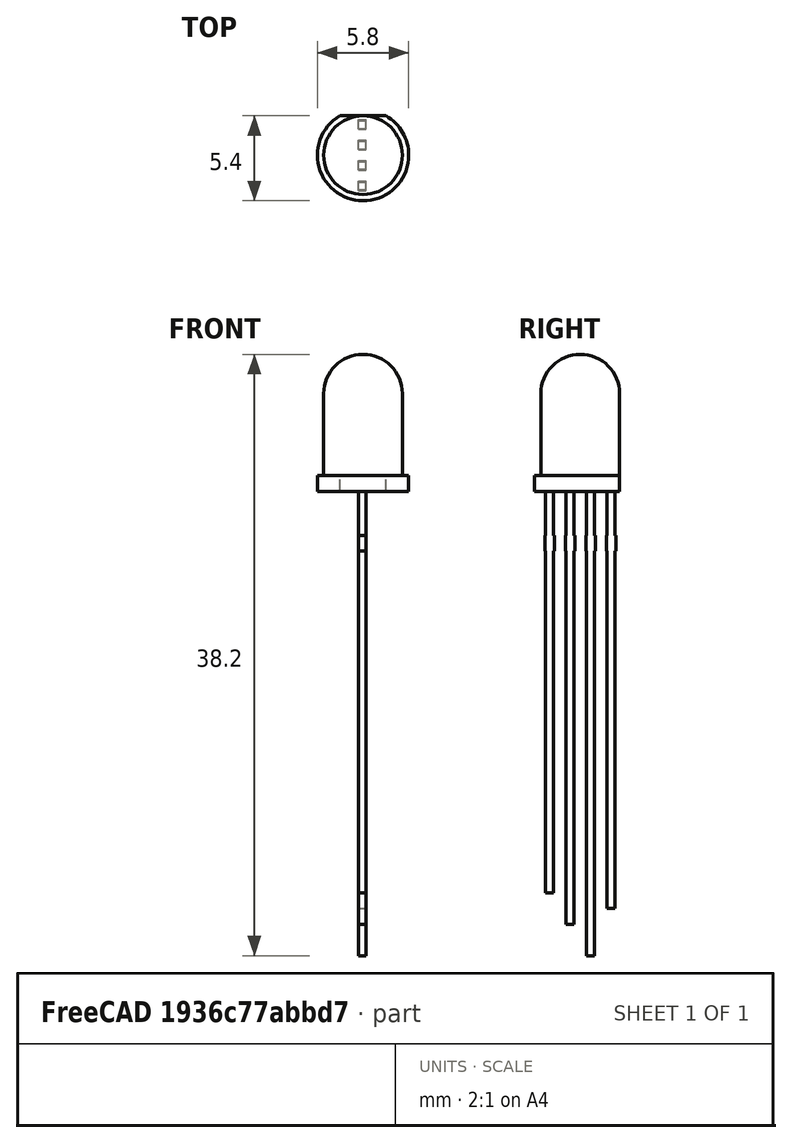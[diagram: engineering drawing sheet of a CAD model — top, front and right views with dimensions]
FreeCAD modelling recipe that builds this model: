
FCSTD DOCUMENT  (FreeCAD 0.16R6703 (Git))
Label: RGB-LED-5mm
License: All rights reserved
LicenseURL: http://en.wikipedia.org/wiki/All_rights_reserved
objects: Part::Box×9, Part::MultiFuse×5, Part::Cylinder×2, Part::Sphere×1, Part::Cut×1
note: 18 computed .brp shape members not serialized (recipe doc carries the construction recipe); baked Part::Feature solids carry a one-line shape summary decoded from their .brp

FEATURE [Part::Cylinder] Cylinder  label="Cilindro"
  Angle = 360
  Height = 5.2
  Placement = pos=(0,0,4.8) rot=(0,0,1;0rad)
  Radius = 2.5
FEATURE [Part::Sphere] Sphere  label="Esfera"
  Angle1 = 0
  Angle2 = 90
  Angle3 = 360
  Placement = pos=(0,0,10) rot=(0,0,1;0rad)
  Radius = 2.5
FEATURE [Part::Cylinder] Cylinder001  label="Cilindro001"
  Angle = 360
  Height = 1
  Placement = pos=(0,0,3.8) rot=(0,0,1;0rad)
  Radius = 2.9
FEATURE [Part::Box] Box  label="Cubo"
  Height = 3
  Length = 13
  Placement = pos=(-4.5,2.5,3) rot=(0,0,1;0rad)
  Width = 2
FEATURE [Part::Box] Box001  label="Cubo001"
  Height = 26.5
  Length = 0.5
  Placement = pos=(0,1.7,-22.7) rot=(0,0,1;0rad)
  Width = 0.5
FEATURE [Part::Box] Box002  label="Cubo002"
  Height = 1
  Length = 0.5
  Placement = pos=(0,1.65,0) rot=(0,0,1;0rad)
  Width = 0.6
FEATURE [Part::Box] Box003  label="GND"
  Height = 29.5
  Length = 0.5
  Placement = pos=(0,0.4,-25.7) rot=(0,0,1;0rad)
  Width = 0.5
FEATURE [Part::Box] Box004  label="Cubo004"
  Height = 27.5
  Length = 0.5
  Placement = pos=(0,-0.9,-23.7) rot=(0,0,1;0rad)
  Width = 0.5
FEATURE [Part::Box] Box005  label="Cubo005"
  Height = 25.5
  Length = 0.5
  Placement = pos=(0,-2.2,-21.7) rot=(0,0,1;0rad)
  Width = 0.5
FEATURE [Part::Cut] Cut  label="Pieza"
  Base = -> Cylinder001
  Tool = -> Box
FEATURE [Part::Box] Box006  label="Cubo006"
  Height = 1
  Length = 0.5
  Placement = pos=(0,0.35,0) rot=(0,0,1;0rad)
  Width = 0.6
FEATURE [Part::Box] Box007  label="Cubo007"
  Height = 1
  Length = 0.5
  Placement = pos=(0,-0.95,0) rot=(0,0,1;0rad)
  Width = 0.6
FEATURE [Part::Box] Box008  label="Cubo008"
  Height = 1
  Length = 0.5
  Placement = pos=(0,-2.25,0) rot=(0,0,1;0rad)
  Width = 0.6
FEATURE [Part::MultiFuse] Fusion  label="Red"
  Shapes = -> [Box001,Box002]
FEATURE [Part::MultiFuse] Fusion001  label="GND001"
  Shapes = -> [Box003,Box006]
FEATURE [Part::MultiFuse] Fusion002  label="Green"
  Shapes = -> [Box004,Box007]
FEATURE [Part::MultiFuse] Fusion003  label="Blue"
  Shapes = -> [Box005,Box008]
FEATURE [Part::MultiFuse] Fusion004  label="Cabeza"
  Placement = pos=(0.3,0,0) rot=(0,0,1;0rad)
  Shapes = -> [Cylinder,Sphere,Cut]
